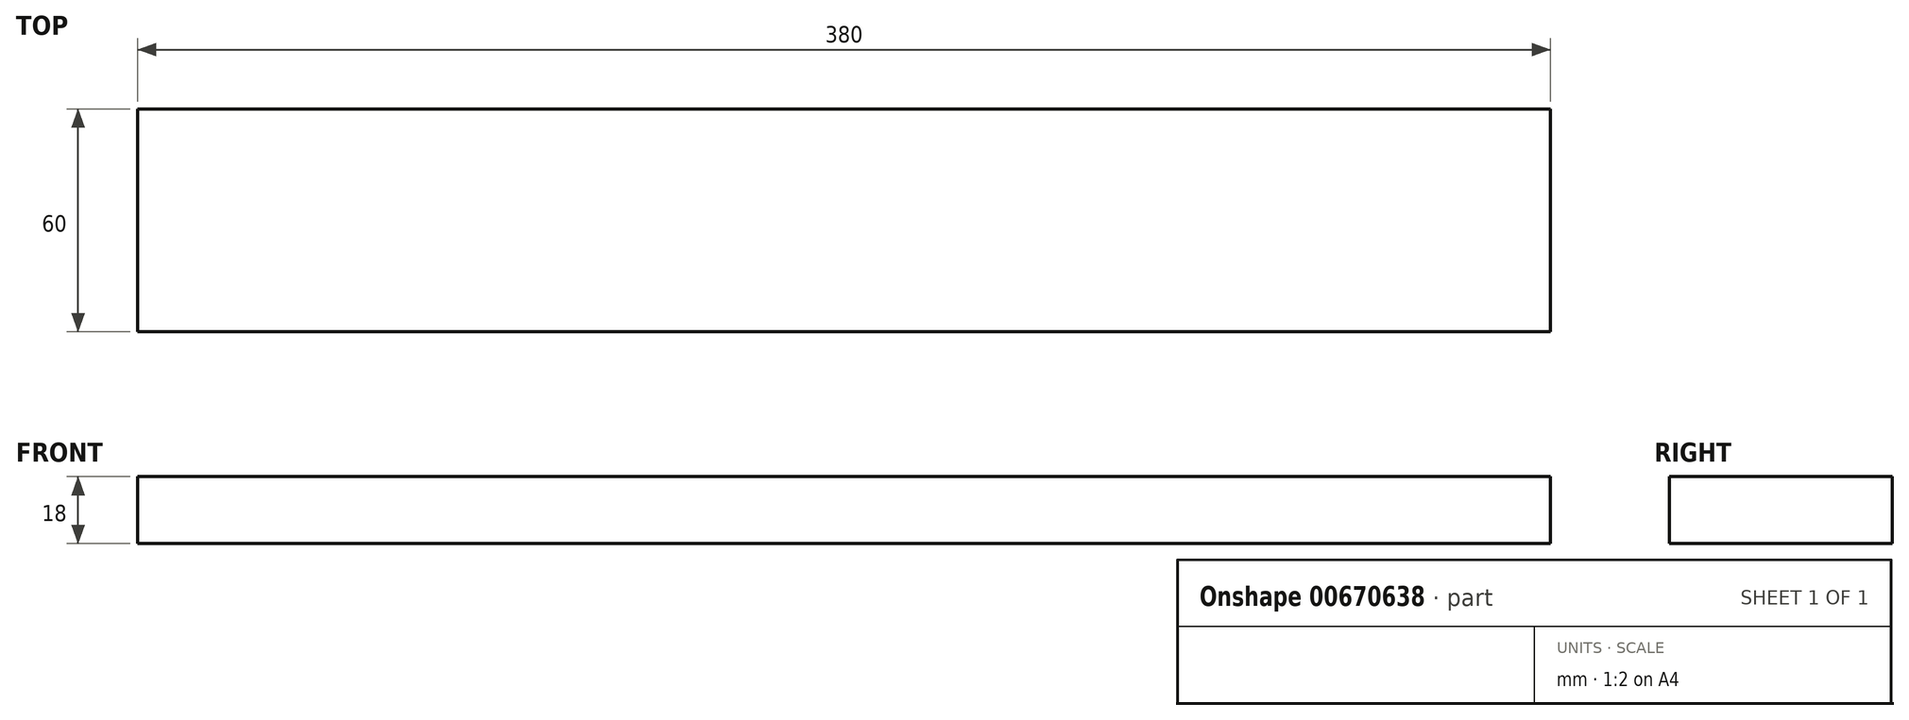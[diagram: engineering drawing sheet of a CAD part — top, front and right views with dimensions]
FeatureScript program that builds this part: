
annotation { "Feature Type Name" : "Feature", "Feature Type Description" : "" }
export const myFeature = defineFeature(function(context is Context, id is Id, definition is map)
    precondition{}
    {
        {
            var Q0;
            Q0=qCreatedBy(makeId("Top.planeOp"),FACE);
            var sketch = newSketch(context, id + "F0", { "sketchPlane" : qUnion([Q0])});
            skLineSegment(sketch, "E0.bottom", {"start": v(190, 30) * mm, "end": v(-190, 30) * mm});
            skLineSegment(sketch, "E0.top", {"start": v(190, -30) * mm, "end": v(-190, -30) * mm});
            skLineSegment(sketch, "E0.left", {"start": v(190, 30) * mm, "end": v(190, -30) * mm});
            skLineSegment(sketch, "E0.right", {"start": v(-190, 30) * mm, "end": v(-190, -30) * mm});
            skPoint(sketch, "E0.middle", {"position": v(0, 0) * mm});
            skSolve(sketch);
        }
        {
            var Q0;
            Q0 = qSketchRegion(id + "F0", true);
            extrude(context, id + "F1", {"entities" : qUnion([Q0]), "endBound" : BoundingType.SYMMETRIC, "depth" : 18 * mm, "offsetDistance" : 25 * mm});
        }
    });
